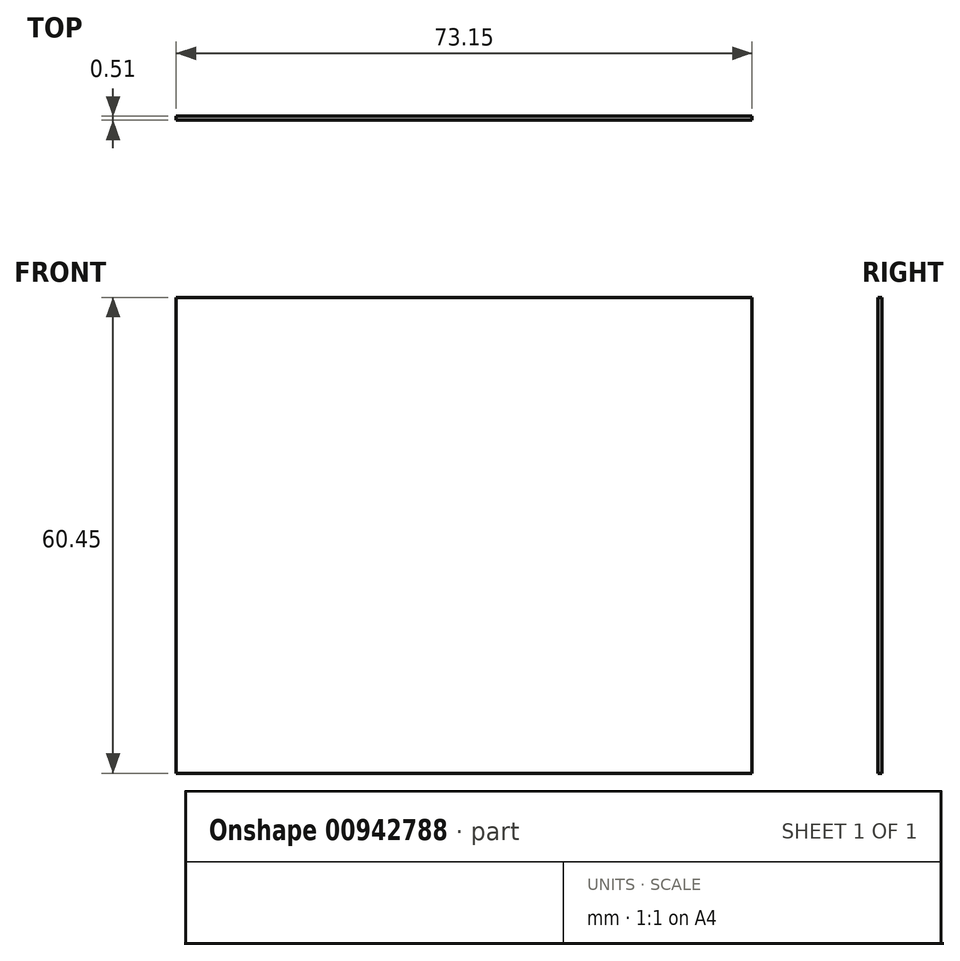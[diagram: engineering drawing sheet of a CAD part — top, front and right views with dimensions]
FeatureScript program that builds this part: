
annotation { "Feature Type Name" : "Feature", "Feature Type Description" : "" }
export const myFeature = defineFeature(function(context is Context, id is Id, definition is map)
    precondition{}
    {
        {
            var Q0;
            Q0=qCreatedBy(makeId("Front.planeOp"),FACE);
            var sketch = newSketch(context, id + "F0", { "sketchPlane" : qUnion([Q0])});
            skLineSegment(sketch, "E0.bottom", {"start": v(0, 0) * mm, "end": v(73.15, 0) * mm});
            skLineSegment(sketch, "E0.top", {"start": v(0, 60.45) * mm, "end": v(73.15, 60.45) * mm});
            skLineSegment(sketch, "E0.left", {"start": v(0, 0) * mm, "end": v(0, 60.45) * mm});
            skLineSegment(sketch, "E0.right", {"start": v(73.15, 0) * mm, "end": v(73.15, 60.45) * mm});
            skSolve(sketch);
        }
        {
            var Q0;
            Q0=makeQuery(id+"F0.imprint","IMPRINT",FACE,{"disambiguationData":[TD([[makeQuery(id+"F0.imprint","IMPRINT",EDGE,{"derivedFrom":sQuery(id+"F0.wireOp",EDGE,"E0.bottom")}),1.0]])]});
            extrude(context, id + "F1", {"entities" : qUnion([Q0]), "depth" : 0.5 * mm, "offsetDistance" : 25.4 * mm});
        }
    });
